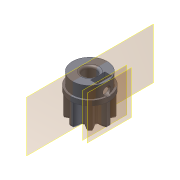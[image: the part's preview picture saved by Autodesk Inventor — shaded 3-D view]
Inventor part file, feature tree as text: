
AUTODESK INVENTOR PART (.ipt)
format: ipt  version: 2015 SP2 (Build 190223200, 223)  size: 374,272 bytes
history: native  units: mm (DEFAULTED — no unit token found)
features: sketch x6, extrude x5, plane x5, other x3, projected_geometry x3, fillet x2, hole x1, reference x1
ambient origin geometry x8: Origin, YZ Plane, XZ Plane, XY Plane, X Axis, Y Axis, Z Axis, Center Point
bodies: Body1 (feature_tree), Body2 (feature_tree)
feature tree (26):
  extrude  "Extrusion1"  Depth=10.0mm TaperAngle=0.0deg
  plane  "Work Plane2"
  plane  "Work Plane8"
  plane  "Work Plane9"
  other  "Engranaje recto"
  extrude  "Extrusión4"  Depth=10.0mm TaperAngle=0.0deg
  hole  "Agujero1"  [1 undecoded]
  plane  "Plano de trabajo11"
  extrude  "Extrusión5"  TaperAngle=0.0deg  [1 undecoded]
  plane  "Plano de trabajo12"
  extrude  "Extrusión6"  Depth=19.0mm
  fillet  "Empalme1"  [1 undecoded]
  fillet  "Empalme2"  Radius=16.8mm
  extrude  "Extrusión7"  Depth=1.0mm
  sketch  "Sketch1"  dims[d0=16.0865mm d1=10.0mm d2=0.0mm]
  sketch  "Sketch2"  dims[d3=13.217391mm d4=10.0mm d5=0.0mm]
  other  "Srf1"
  sketch  "Boceto6"  dims[d16=19.0mm d17=0.0mm d34=22.5deg]
  sketch  "Boceto7"  dims[d39=0.0mm d41=0.0mm]
  projected_geometry  "Contorno proyectado1"
  sketch  "Boceto8"  dims[d43=19.0mm d46=19.0mm d47=0.0mm d48=0.0mm d55=16.8mm]
  projected_geometry  "Contorno proyectado2"
  projected_geometry  "Contorno proyectado3"
  sketch  "Boceto9"  dims[d56=7.0mm d57=0.0mm d80=10.0mm d81=10.0mm d60=5.7mm d61=6.0mm d62=4.0mm d63=2.0mm d64=90.0deg d65=8.0mm d66=20.594885mm d67=3.45mm d68=7.0mm d69=0.0mm d70=-2.0mm d71=6.2mm d72=2.0mm d73=3.0mm d74=0.0mm d78=1.0mm d79=1.0mm d82=15.0mm d83=5.0mm d84=0.0mm]
  reference  "Referencia1"
  other  "Diámetro de separación"
note: 3 required parameter values undecoded (feature->parameter linkage not recoverable at this tier; creation-order binding heuristic only, values carry confidence <= 0.55)
